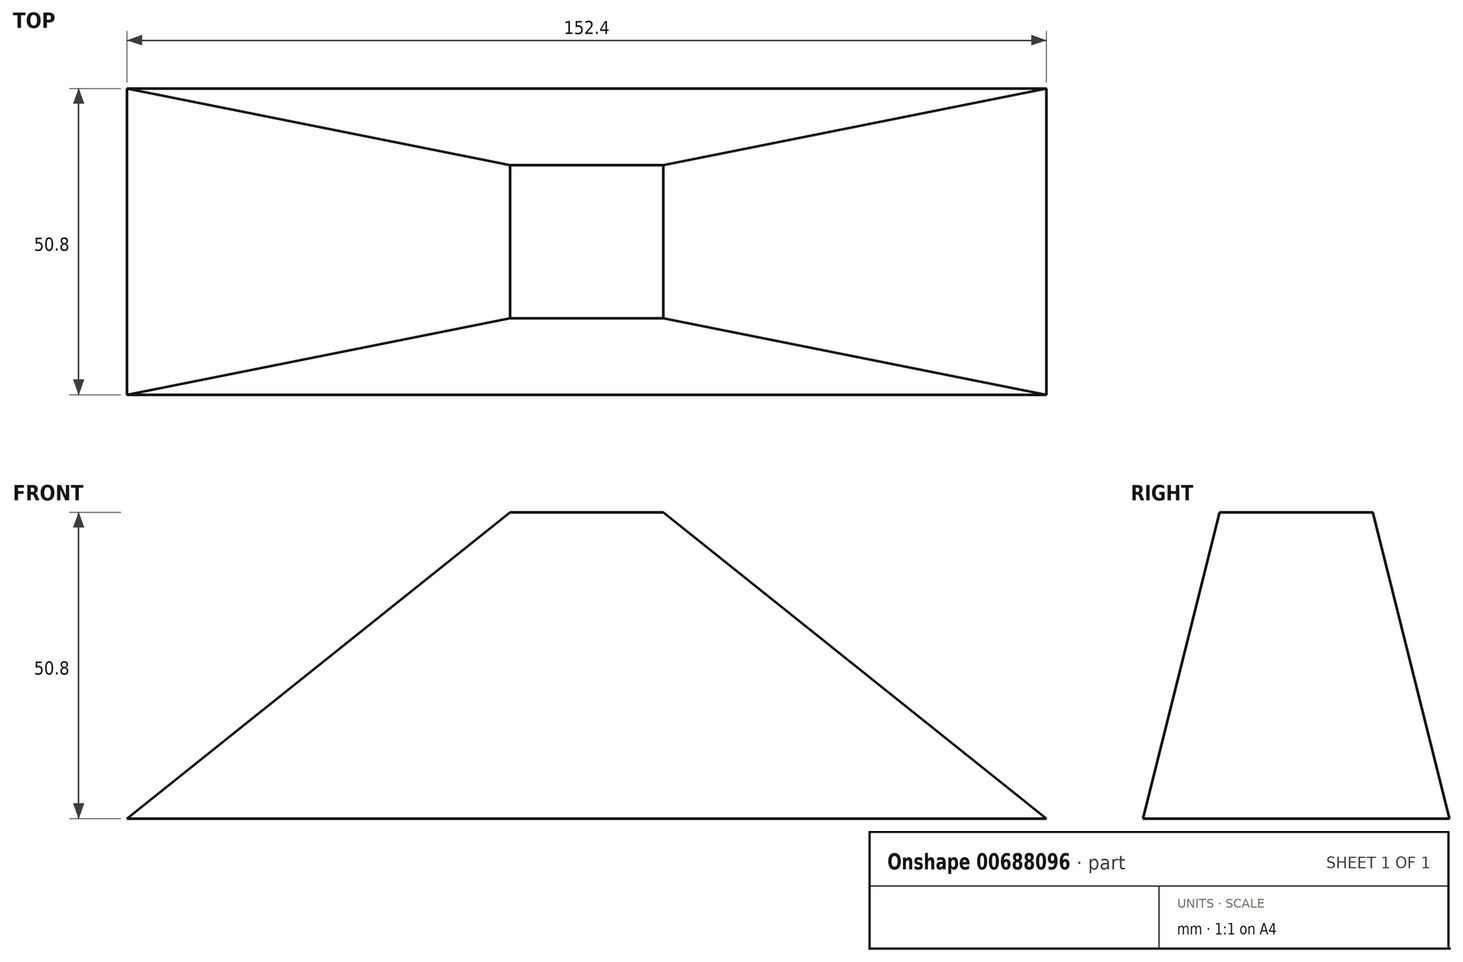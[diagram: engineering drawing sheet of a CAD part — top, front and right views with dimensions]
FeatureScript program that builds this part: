
annotation { "Feature Type Name" : "Feature", "Feature Type Description" : "" }
export const myFeature = defineFeature(function(context is Context, id is Id, definition is map)
    precondition{}
    {
        {
            var Q0;
            Q0=qCreatedBy(makeId("Top.planeOp"),FACE);
            var sketch = newSketch(context, id + "F0", { "sketchPlane" : qUnion([Q0])});
            skLineSegment(sketch, "E0.bottom", {"start": v(76.2, -25.4) * mm, "end": v(-76.2, -25.4) * mm});
            skLineSegment(sketch, "E0.top", {"start": v(76.2, 25.4) * mm, "end": v(-76.2, 25.4) * mm});
            skLineSegment(sketch, "E0.left", {"start": v(76.2, -25.4) * mm, "end": v(76.2, 25.4) * mm});
            skLineSegment(sketch, "E0.right", {"start": v(-76.2, -25.4) * mm, "end": v(-76.2, 25.4) * mm});
            skPoint(sketch, "E0.middle", {"position": v(0, 0) * mm});
            skSolve(sketch);
        }
        {
            var Q0;
            Q0=qCreatedBy(makeId("Top.planeOp"),FACE);
            cPlane(context, id + "F1", {"entities" : qUnion([Q0]), "cplaneType" : CPlaneType.OFFSET, "offset" : 50.8 * mm, "width" : 152.4 * mm, "height" : 152.4 * mm});
        }
        {
            var Q0;
            Q0=qCreatedBy(id+"F1.planeOp",FACE);
            var sketch = newSketch(context, id + "F2", { "sketchPlane" : qUnion([Q0])});
            skLineSegment(sketch, "E1.bottom", {"start": v(12.7, -12.7) * mm, "end": v(-12.7, -12.7) * mm});
            skLineSegment(sketch, "E1.top", {"start": v(12.7, 12.7) * mm, "end": v(-12.7, 12.7) * mm});
            skLineSegment(sketch, "E1.left", {"start": v(12.7, -12.7) * mm, "end": v(12.7, 12.7) * mm});
            skLineSegment(sketch, "E1.right", {"start": v(-12.7, -12.7) * mm, "end": v(-12.7, 12.7) * mm});
            skPoint(sketch, "E1.middle", {"position": v(0, 0) * mm});
            skSolve(sketch);
        }
        {
            var Q0;
            Q0=makeQuery(id+"F0.imprint","IMPRINT",FACE,{"disambiguationData":[TD([[makeQuery(id+"F0.imprint","IMPRINT",EDGE,{"derivedFrom":sQuery(id+"F0.wireOp",EDGE,"E0.bottom")}),-1.0]])]});
            var Q1;
            Q1=makeQuery(id+"F2.imprint","IMPRINT",FACE,{"disambiguationData":[TD([[makeQuery(id+"F2.imprint","IMPRINT",EDGE,{"derivedFrom":sQuery(id+"F2.wireOp",EDGE,"E1.bottom")}),-1.0]])]});
            loft(context, id + "F3", {"sheetProfilesArray" : [{ "sheetProfileEntities" : qUnion([Q0]) }, { "sheetProfileEntities" : qUnion([Q1]) }]});
        }
    });
